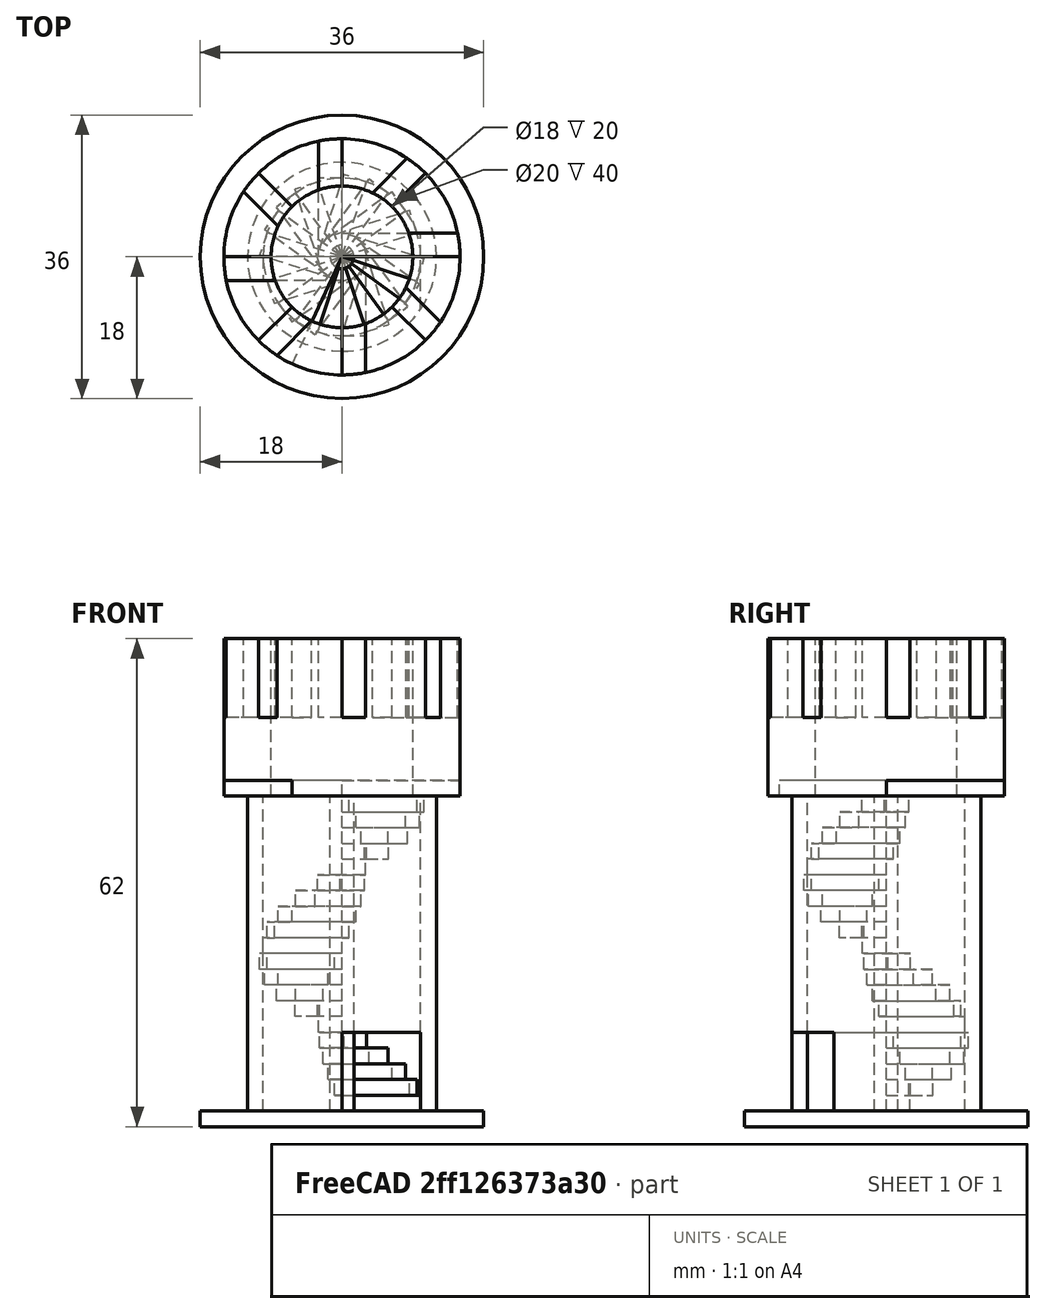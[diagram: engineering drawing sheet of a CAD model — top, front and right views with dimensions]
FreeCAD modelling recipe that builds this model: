
FCSTD DOCUMENT  (FreeCAD 0.17R13247 (Git))
Label: TorreCastillo
License: CreativeCommons Attribution-ShareAlike
LicenseURL: http://creativecommons.org/licenses/by-sa/4.0/
objects: Part::Cylinder×7, Part::Cut×4, Part::Box×3, Part::FeaturePython×2, Spreadsheet::Sheet×1
note: 16 computed .brp shape members not serialized (recipe doc carries the construction recipe); baked Part::Feature solids carry a one-line shape summary decoded from their .brp

FEATURE [Part::Box] Box  label="Peldano-inicial"
  AttacherType = Attacher::AttachEngine3D
  Height = 2
  Length = 10
  Width = 3
  expr: Height = Spreadsheet.peldano_alto
  expr: Width = Spreadsheet.peldano_profundidad
  expr: Length = Spreadsheet.peldano_ancho
FEATURE [Part::FeaturePython] Array  label="Escalera"  # Draft array (typed FeaturePython)
  Angle = 360
  ArrayType = 1
  Axis = (0,0,1)
  Base = -> Box
  Center = (0,0,0)
  Fuse = false
  IntervalAxis = (0,0,2)
  IntervalX = (1,0,0)
  IntervalY = (1,0,0)
  IntervalZ = (0,0,0)
  NumberPolar = 20
  NumberX = 3
  NumberY = 2
  NumberZ = 1
  expr: IntervalAxis.z = Spreadsheet.peldano_alto
  expr: NumberY = Spreadsheet.peldano_alto
  expr: NumberPolar = Spreadsheet.Altura
FEATURE [Part::Cylinder] Cylinder  label="guia-escalera"
  Angle = 360
  AttacherType = Attacher::AttachEngine3D
  Height = 40
  Radius = 1.5
  expr: Height = Spreadsheet.Altura * Spreadsheet.peldano_alto
FEATURE [Spreadsheet::Sheet] Spreadsheet
  cells = A1=Datos; A2=Altura escalera; B2(Altura)=20; A3=Ancho peldaño; B3(peldano_ancho)=10; A4=Alto peldaño; B4(peldano_alto)=2; A5=Profundidad peldaño; B5(peldano_profundidad)=3
FEATURE [Part::Cylinder] Cylinder001  label="Cilindro"
  Angle = 360
  AttacherType = Attacher::AttachEngine3D
  Height = 40
  Radius = 10
  expr: Radius = Spreadsheet.peldano_ancho
  expr: Height = Spreadsheet.Altura * Spreadsheet.peldano_alto
FEATURE [Part::Cylinder] Cylinder002  label="Cilindro001"
  Angle = 360
  AttacherType = Attacher::AttachEngine3D
  Height = 40
  Radius = 12
  expr: Radius = Spreadsheet.peldano_ancho * 1.2
  expr: Height = Spreadsheet.Altura * Spreadsheet.peldano_alto
FEATURE [Part::Cut] Cut
  Base = -> Cylinder002
  Refine = true
  Tool = -> Cylinder001
FEATURE [Part::Box] Box001  label="Cubo"
  AttacherType = Attacher::AttachEngine3D
  Height = 10
  Length = 10
  Placement = pos=(0,-20,0) rot=(0,0,1;0rad)
  Width = 20
  expr: Width = Spreadsheet.peldano_ancho * 2
  expr: Length = Spreadsheet.peldano_ancho
  expr: Placement.Base.y = -Spreadsheet.peldano_ancho * 2
FEATURE [Part::Cut] Cut001  label="Exterior-torre"
  Base = -> Cut
  Refine = true
  Tool = -> Box001
FEATURE [Part::Cylinder] Cylinder003  label="Base"
  Angle = 360
  AttacherType = Attacher::AttachEngine3D
  Height = 2
  Placement = pos=(0,0,-2) rot=(0,0,1;0rad)
  Radius = 18
  expr: Radius = Spreadsheet.peldano_ancho * 1.8
FEATURE [Part::Cylinder] Cylinder004  label="Cilindro002"
  Angle = 360
  AttacherType = Attacher::AttachEngine3D
  Height = 20
  Placement = pos=(0,0,40) rot=(0,0,1;0rad)
  Radius = 15
  expr: Placement.Base.z = Spreadsheet.Altura * Spreadsheet.peldano_alto
  expr: Height = 10 * Spreadsheet.peldano_alto
  expr: Radius = Spreadsheet.peldano_ancho * 1.5
FEATURE [Part::Cylinder] Cylinder005  label="Cilindro003"
  Angle = 360
  AttacherType = Attacher::AttachEngine3D
  Height = 20
  Placement = pos=(0,0,40) rot=(0,0,1;0rad)
  Radius = 9
  expr: Radius = Spreadsheet.peldano_ancho * 0.90000000000000002
  expr: Height = 10 * Spreadsheet.peldano_alto
  expr: Placement.Base.z = Spreadsheet.Altura * Spreadsheet.peldano_alto
FEATURE [Part::Cut] Cut002  label="torre-superior"
  Base = -> Cylinder004
  Refine = true
  Tool = -> Cylinder005
FEATURE [Part::Cylinder] Cylinder006  label="Base-superior"
  Angle = 245
  AttacherType = Attacher::AttachEngine3D
  Height = 2
  Placement = pos=(0,0,40) rot=(0,0,1;0rad)
  Radius = 15
  expr: Placement.Base.z = Spreadsheet.Altura * Spreadsheet.peldano_alto
  expr: Radius = Spreadsheet.peldano_ancho * 1.5
FEATURE [Part::Box] Box002  label="Cubo001"
  AttacherType = Attacher::AttachEngine3D
  Height = 100
  Length = 20
  Placement = pos=(7,0,50) rot=(0,0,1;0rad)
  Width = 3
  expr: Length = Spreadsheet.peldano_ancho * 2
  expr: Height = Spreadsheet.peldano_ancho * 10
  expr: Width = Spreadsheet.peldano_profundidad
  expr: Placement.Base.z = Spreadsheet.Altura * Spreadsheet.peldano_alto + Spreadsheet.peldano_alto * 5
FEATURE [Part::FeaturePython] Array001  label="Almenas"  # Draft array (typed FeaturePython)
  Angle = 360
  ArrayType = 1
  Axis = (0,0,1)
  Base = -> Box002
  Center = (0,0,0)
  Fuse = false
  IntervalAxis = (0,0,0)
  IntervalX = (1,0,0)
  IntervalY = (0,1,0)
  IntervalZ = (0,0,0)
  NumberPolar = 8
  NumberX = 2
  NumberY = 2
  NumberZ = 1
FEATURE [Part::Cut] Cut003  label="parte-superior"
  Base = -> Cut002
  Refine = true
  Tool = -> Array001
